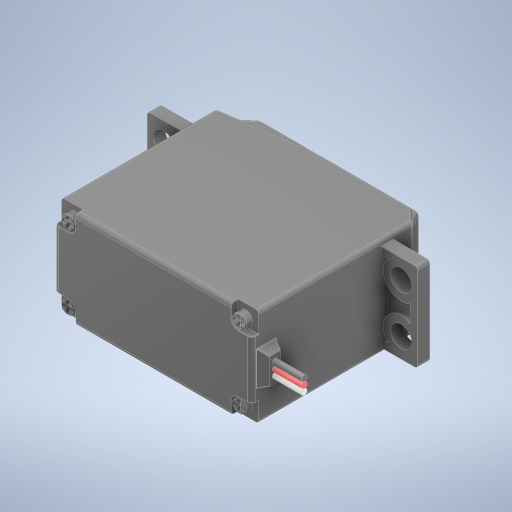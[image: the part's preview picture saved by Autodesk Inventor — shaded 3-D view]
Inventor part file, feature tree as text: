
AUTODESK INVENTOR PART (.ipt)
format: ipt  version: 2023 (Build 270158000, 158)  size: 568,832 bytes
history: mixed  units: mm
features: other x1, extrude x1, imported_body x1
ambient origin geometry x8: Origin, YZ Plane, XZ Plane, XY Plane, X Axis, Y Axis, Z Axis, Center Point
bodies: Body1 (imported_parasolid)
feature tree (3):
  other  "Sólido1"
  extrude  "Extrude26"  [1 undecoded]
  imported_body  NMx_Import_Brep_tag  [imported B-rep: ~8 faces, bbox_mm=[0.0, 5.140031, 0.0]]
note: 1 required parameter value undecoded (feature->parameter linkage not recoverable at this tier; creation-order binding heuristic only, values carry confidence <= 0.55)
